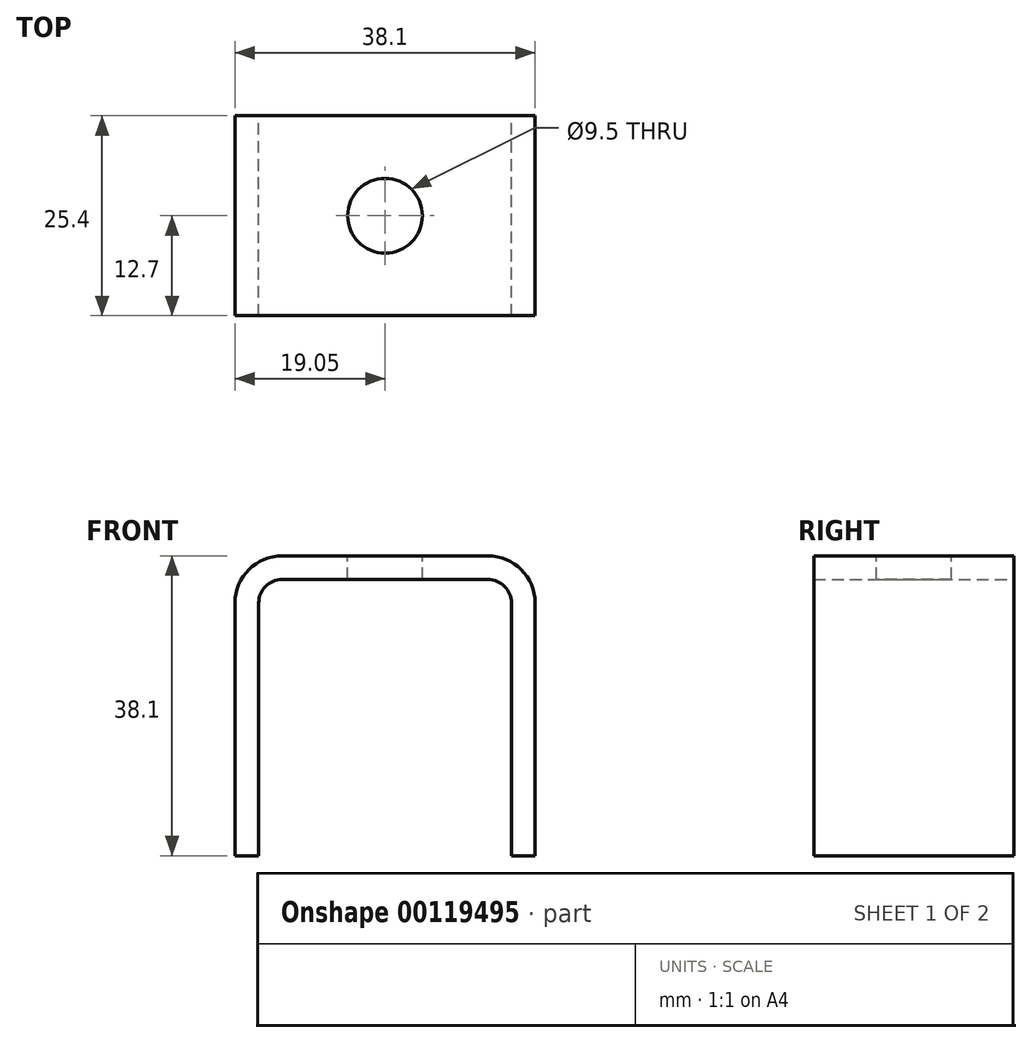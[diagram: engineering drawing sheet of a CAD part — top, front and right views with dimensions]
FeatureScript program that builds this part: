
annotation { "Feature Type Name" : "Feature", "Feature Type Description" : "" }
export const myFeature = defineFeature(function(context is Context, id is Id, definition is map)
    precondition{}
    {
        {
            var Q0;
            Q0=qCreatedBy(makeId("Front.planeOp"),FACE);
            var sketch = newSketch(context, id + "F0", { "sketchPlane" : qUnion([Q0])});
            skLineSegment(sketch, "E0.bottom", {"start": v(-13.05, 0) * mm, "end": v(13.05, 0) * mm});
            skLineSegment(sketch, "E0.left", {"start": v(-19.05, -6) * mm, "end": v(-19.05, -38.1) * mm});
            skLineSegment(sketch, "E0.right", {"start": v(19.05, -6) * mm, "end": v(19.05, -38.1) * mm});
            skLineSegment(sketch, "E1.bottom", {"start": v(-13.05, -3) * mm, "end": v(13.05, -3) * mm});
            skLineSegment(sketch, "E1.left", {"start": v(-16.05, -6) * mm, "end": v(-16.05, -38.1) * mm});
            skLineSegment(sketch, "E1.right", {"start": v(16.05, -6) * mm, "end": v(16.05, -38.1) * mm});
            skLineSegment(sketch, "E2", {"start": v(-19.05, -38.1) * mm, "end": v(-16.05, -38.1) * mm});
            skLineSegment(sketch, "E3", {"start": v(16.05, -38.1) * mm, "end": v(19.05, -38.1) * mm});
            skPoint(sketch, "E4.visualSharp", {"position": v(-16.05, -3) * mm});
            skArc(sketch, "E4.filletArc", {"start": v(-13.05, -3) * mm, "mid": v(-15.17, -3.88) * mm, "end": v(-16.05, -6) * mm});
            skPoint(sketch, "E5.visualSharp", {"position": v(16.05, -3) * mm});
            skArc(sketch, "E5.filletArc", {"start": v(16.05, -6) * mm, "mid": v(15.17, -3.88) * mm, "end": v(13.05, -3) * mm});
            skPoint(sketch, "E6.visualSharp", {"position": v(19.05, 0) * mm});
            skArc(sketch, "E6.filletArc", {"start": v(19.05, -6) * mm, "mid": v(17.3, -1.76) * mm, "end": v(13.05, 0) * mm});
            skPoint(sketch, "E7.visualSharp", {"position": v(-19.05, 0) * mm});
            skArc(sketch, "E7.filletArc", {"start": v(-13.05, 0) * mm, "mid": v(-17.3, -1.76) * mm, "end": v(-19.05, -6) * mm});
            skSolve(sketch);
        }
        {
            var Q0;
            Q0=makeQuery(id+"F0.imprint","IMPRINT",FACE,{"disambiguationData":[TD([[makeQuery(id+"F0.imprint","IMPRINT",EDGE,{"derivedFrom":sQuery(id+"F0.wireOp",EDGE,"E0.bottom")}),-1.0]])]});
            extrude(context, id + "F1", {"entities" : qUnion([Q0]), "endBound" : BoundingType.SYMMETRIC, "depth" : 25.4 * mm});
        }
        {
            var Q0;
            Q0=makeQuery(id+"F1.opExtrude","SWEPT_FACE",FACE,{"disambiguationData":[OSD([sQuery(id+"F0.wireOp",EDGE,"E0.bottom")])]});
            var sketch = newSketch(context, id + "F2", { "sketchPlane" : qUnion([Q0])});
            skPoint(sketch, "E8", {"position": v(0, 0) * mm});
            skSolve(sketch);
        }
        {
            var Q0;
            Q0=sQuery(id+"F2.wireOp",VERTEX,"E8");
            var Q1;
            Q1=makeQuery(id+"F1.opExtrude","SWEPT_BODY",BODY,{"disambiguationData":[OSD([sQuery(id+"F0.wireOp",EDGE,"E0.bottom"),sQuery(id+"F0.wireOp",EDGE,"E0.left"),sQuery(id+"F0.wireOp",EDGE,"E0.right"),sQuery(id+"F0.wireOp",EDGE,"E1.bottom"),sQuery(id+"F0.wireOp",EDGE,"E1.left"),sQuery(id+"F0.wireOp",EDGE,"E1.right"),sQuery(id+"F0.wireOp",EDGE,"E2"),sQuery(id+"F0.wireOp",EDGE,"E3"),sQuery(id+"F0.wireOp",EDGE,"E4.filletArc"),sQuery(id+"F0.wireOp",EDGE,"E5.filletArc"),sQuery(id+"F0.wireOp",EDGE,"E6.filletArc"),sQuery(id+"F0.wireOp",EDGE,"E7.filletArc")])]});
            hole(context, id + "F3", {"style" : HoleStyle.SIMPLE, "endStyle" : HoleEndStyle.THROUGH, "holeDiameter" : 9.5 * mm, "locations" : qUnion([Q0]), "scope" : qUnion([Q1]), "isTappedThrough" : true});
        }
    });
